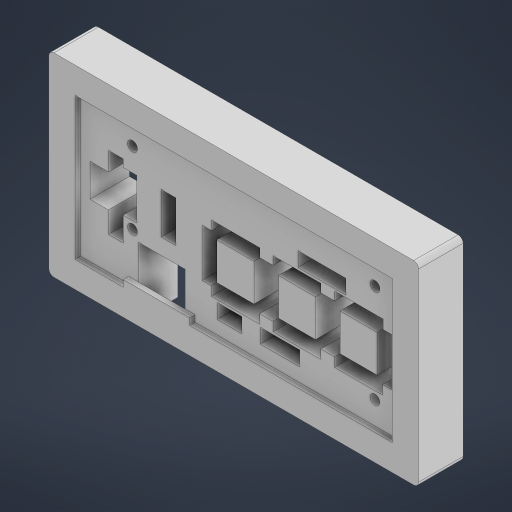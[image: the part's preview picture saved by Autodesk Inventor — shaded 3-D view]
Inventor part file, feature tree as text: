
AUTODESK INVENTOR PART (.ipt)
format: ipt  version: 2024.1 (Build 281209000, 209)  size: 5,024,768 bytes
history: native  units: mm
features: projected_geometry x7, extrude x5, sketch x5, other x2, plane x1, fillet x1
ambient origin geometry x8: Origin, YZ Plane, XZ Plane, XY Plane, X Axis, Y Axis, Z Axis, Center Point
bodies: Solid1 (feature_tree)
feature tree (21):
  other  "3D_PCB1_2024-08-12"
  extrude  "Extrusion1"  Depth=10.0mm
  sketch  "Sketch2"  dims[d2=2.0mm d3=2.0mm]
  plane  "Work Plane1"
  extrude  "Extrusion2"  Depth=2.0mm
  extrude  "Extrusion3"  Depth=1.0mm
  extrude  "Extrusion4"  Depth=1.0mm
  fillet  "Fillet1"  Radius=1.0mm
  extrude  "Extrusion5"  Depth=10.0mm
  sketch  "Sketch1"  dims[d0=2.0mm d1=10.0mm]
  sketch  "Sketch3"  dims[d4=2.5mm d5=1.0mm]
  sketch  "Sketch4"  dims[d6=1.0mm d7=1.0mm d10=1.0mm]
  sketch  "Sketch5"  dims[d11=1.0mm d12=1.0mm d13=1.0mm d14=1.0mm d15=1.0mm d16=1.0mm d17=1.0mm d18=1.0mm d19=1.0mm d20=1.0mm d21=1.0mm d22=1.0mm d23=1.0mm d24=1.0mm d25=1.0mm d26=1.0mm d27=1.0mm d28=1.0mm d29=1.0mm d30=1.0mm d31=1.0mm d32=1.0mm d33=1.0mm d34=1.0mm d35=1.0mm d36=1.0mm d37=1.0mm d38=1.0mm d39=1.0mm d40=1.0mm d41=1.0mm d42=1.0mm d43=1.0mm d44=1.0mm d45=1.0mm d46=1.0mm d47=1.0mm d48=1.0mm d49=1.0mm d50=1.0mm d51=1.0mm d52=1.0mm d53=1.0mm d54=1.0mm d55=1.0mm d56=1.0mm d57=1.0mm d58=1.0mm d59=1.0mm d60=1.0mm d61=1.0mm d62=1.0mm d63=1.0mm d64=1.0mm d65=1.0mm d66=1.0mm d67=3.0mm d68=3.0mm d69=3.0mm d70=3.0mm d71=10.0mm d72=0.0mm d73=2.0mm d74=0.0mm d75=10.0mm d76=0.0mm d77=3.0mm d78=3.0mm d79=10.0mm d80=0.0mm d81=7.853982mm d82=1.5mm d83=3.0mm d85=1.590604mm d86=1.590604mm d87=2.0mm d88=0.0mm d89=135.0deg d90=1.590604mm d91=18.796039mm d92=30.0mm d94=18.796039mm d95=10.0mm d97=10.0mm d99=1.5mm d100=10.0mm d101=0.0mm]
  projected_geometry  "Projected Loop1"
  projected_geometry  "Projected Loop2"
  projected_geometry  "Projected Loop3"
  projected_geometry  "Projected Loop4"
  projected_geometry  "Projected Loop5"
  projected_geometry  "Projected Loop6"
  projected_geometry  "Projected Loop7"
  other  "3D_PCB1_2024-08-12.obj"
